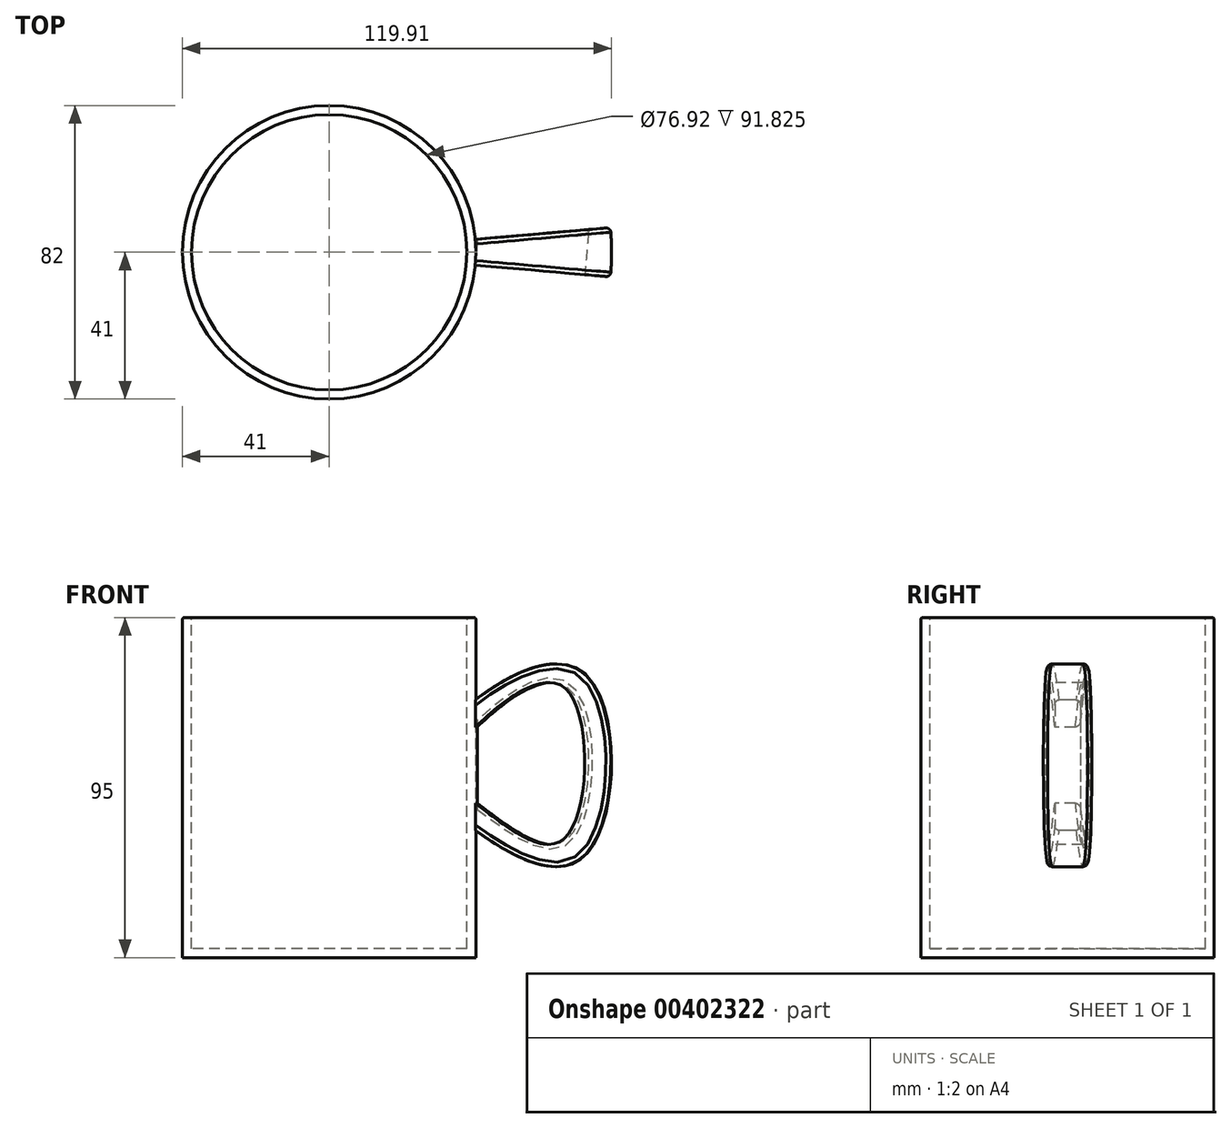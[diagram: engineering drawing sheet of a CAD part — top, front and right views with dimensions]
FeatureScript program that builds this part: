
annotation { "Feature Type Name" : "Feature", "Feature Type Description" : "" }
export const myFeature = defineFeature(function(context is Context, id is Id, definition is map)
    precondition{}
    {
        {
            var Q0;
            Q0=qCreatedBy(makeId("Top.planeOp"),FACE);
            var sketch = newSketch(context, id + "F0", { "sketchPlane" : qUnion([Q0])});
            skCircle(sketch, "E0", {"center": v(0, 0) * mm, "radius": 41 * mm});
            skSolve(sketch);
        }
        {
            var Q0;
            Q0 = qSketchRegion(id + "F0", true);
            extrude(context, id + "F1", {"entities" : qUnion([Q0]), "oppositeDirection" : true, "depth" : 95 * mm});
        }
        {
            var Q0;
            Q0=makeQuery(id+"F1.opExtrude","CAP_FACE",FACE,{"disambiguationData":[OSD([sQuery(id+"F0.wireOp",EDGE,"E0")])],"isStart":true});
            shell(context, id + "F2", {"entities" : qUnion([Q0]), "thickness" : 2.54 * mm});
        }
        {
            var Q0;
            Q0=qCreatedBy(makeId("Front.planeOp"),FACE);
            var sketch = newSketch(context, id + "F3", { "sketchPlane" : qUnion([Q0])});
            skFitSpline(sketch, "E1", {"points": [v(33.38, -29.47) * mm, v(71.48, -15.7) * mm, v(71.48, -66.52) * mm, v(33.38, -53.56) * mm], "startDerivative": vector(106.89, 102) * mm, "endDerivative": vector(-128.5, 105.84) * mm});
            skLineSegment(sketch, "E2", {"start": v(41, 0) * mm, "end": v(41, -95) * mm});
            skLineSegment(sketch, "E3", {"start": v(0, 0) * mm, "end": v(0, -95) * mm});
            skSolve(sketch);
        }
        {
            var Q0;
            Q0 = qSketchRegion(id + "F3", true);
            var Q1;
            Q1=sQuery(id+"F3.wireOp",EDGE,"E3");
            revolve(context, id + "F4", {"operationType" : NewBodyOperationType.ADD, "entities" : qUnion([Q0]), "axis" : qUnion([Q1]), "revolveType" : RevolveType.SYMMETRIC, "oppositeDirection" : true, "angle" : 10 * degree});
        }
        {
            var Q0;
            Q0=makeQuery(id+"F4.opRevolve","CAP_FACE",FACE,{"disambiguationData":[OSD([sQuery(id+"F3.wireOp",EDGE,"E1"),sQuery(id+"F3.wireOp",EDGE,"E2")])],"isStart":true});
            var sketch = newSketch(context, id + "F5", { "sketchPlane" : qUnion([Q0])});
            skFitSpline(sketch, "E4", {"points": [v(41, -30.6) * mm, v(66.4, -19.97) * mm, v(66.4, -61.32) * mm, v(41, -51.87) * mm], "startDerivative": vector(80.04, 77.08) * mm, "endDerivative": vector(-98.43, 76.15) * mm});
            skSolve(sketch);
        }
        {
            var Q0;
            {var subQ0=sQuery(id+"F5.wireOp",EDGE,"E4");Q0=makeQuery(id+"F5.imprint","IMPRINT",FACE,{"disambiguationData":[TD([[makeQuery(id+"F5.imprint","IMPRINT",EDGE,{"derivedFrom":subQ0}),-1.0]])]});}
            extrude(context, id + "F6", {"entities" : qUnion([Q0]), "operationType" : NewBodyOperationType.REMOVE, "oppositeDirection" : true, "depth" : 25.4 * mm});
        }
        {
            var Q0;
            Q0=makeQuery(id+"F1.opExtrude","CAP_EDGE",EDGE,{"disambiguationData":[OSD([sQuery(id+"F0.wireOp",EDGE,"E0")])],"isStart":true});
            var Q1;
            {var subQ0=sQuery(id+"F0.wireOp",EDGE,"E0");Q1=makeQuery(id+"F2.opShell","OFFSET_EDGE",EDGE,{"disambiguationData":[OSD([subQ0]),TDD([makeQuery(id+"F1.opExtrude","CAP_EDGE",EDGE,{"disambiguationData":[OSD([subQ0])],"isStart":true})])]});}
            fillet(context, id + "F7", {"entities" : qUnion([Q0, Q1]), "radius" : 0.64 * mm, "tangentPropagation" : true, "allowEdgeOverflow" : false});
        }
        {
            var Q0;
            Q0=makeQuery(id+"F6.boolean.opBoolean","COPY",EDGE,{"derivedFrom":makeQuery(id+"F6.opExtrude","CAP_EDGE",EDGE,{"disambiguationData":[OSD([sQuery(id+"F5.wireOp",EDGE,"E4")])],"isStart":true})});
            var Q1;
            Q1=makeQuery(id+"F4.opRevolve","CAP_EDGE",EDGE,{"disambiguationData":[OSD([sQuery(id+"F3.wireOp",EDGE,"E1")])],"isStart":true});
            var Q2;
            Q2=makeQuery(id+"F4.opRevolve","CAP_EDGE",EDGE,{"disambiguationData":[OSD([sQuery(id+"F3.wireOp",EDGE,"E1")])],"isStart":false});
            var Q3;
            Q3=makeQuery(id+"F6.boolean.opBoolean","INTERSECT",EDGE,{"derivedFrom":[makeQuery(id+"F4.opRevolve","CAP_FACE",FACE,{"disambiguationData":[OSD([sQuery(id+"F3.wireOp",EDGE,"E1"),sQuery(id+"F3.wireOp",EDGE,"E2")])],"isStart":false}),makeQuery(id+"F6.opExtrude","SWEPT_FACE",FACE,{"disambiguationData":[OSD([sQuery(id+"F5.wireOp",EDGE,"E4")])]})]});
            fillet(context, id + "F8", {"entities" : qUnion([Q0, Q1, Q2, Q3]), "radius" : 1.27 * mm, "tangentPropagation" : true, "allowEdgeOverflow" : false});
        }
    });
